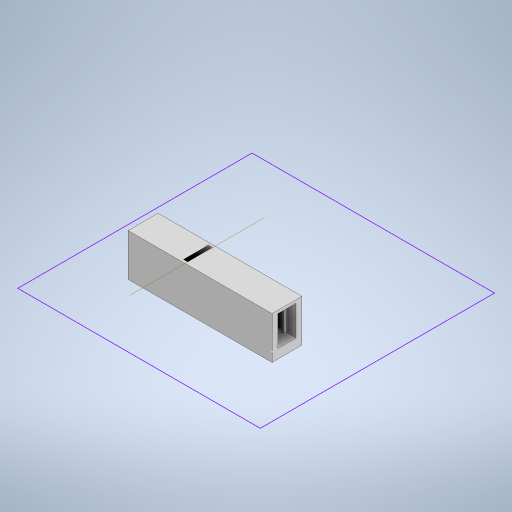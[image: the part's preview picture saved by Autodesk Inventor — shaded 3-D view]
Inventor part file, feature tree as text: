
AUTODESK INVENTOR PART (.ipt)
format: ipt  version: 2023 (Build 270158000, 158)  size: 439,296 bytes
history: native  units: in
note: dims shown in document units (in); Inventor stores cm internally (conversion verified against a paired STEP export)
features: sketch x8, extrude x7, plane x1
ambient origin geometry x8: Origin, YZ Plane, XZ Plane, XY Plane, X Axis, Y Axis, Z Axis, Center Point
bodies: Solid1 (feature_tree)
feature tree (16):
  extrude  "Extrusion1"  Depth=1.25in
  extrude  "Extrusion2"  Depth=0.55in
  extrude  "Extrusion3"  Depth=0.07in TaperAngle=0.0deg
  extrude  "Extrusion4"  TaperAngle=0.0deg  [1 undecoded]
  extrude  "Extrusion5"  Depth=0.0625in
  extrude  "Extrusion6"  Depth=0.25in
  plane  "Work Plane1"
  extrude  "Extrusion7"  Depth=0.1in
  sketch  "Sketch8"  dims[d17=0.1in d18=0.1in d19=0.1in d20=0.1in d21=1.0in d22=0.1in d23=0.1in d24=0.1in d25=0.1in d26=0.1in d27=0.1in d28=0.1in d29=0.1in d30=0.1in d31=0.1in d32=0.1in d33=0.1in d34=1.0in d35=1.0in d36=1.0in d37=1.25in d38=0.0in d39=0.1in d40=0.1in d41=0.1in d42=0.1in d43=0.1in d44=0.1in d45=1.0in d46=1.0in d47=0.1in d48=0.1in d49=1.0in d50=0.1in d51=0.1in d52=1.0in d53=1.25in d54=0.0in d55=0.125in d56=0.0in d57=45.0deg d58=0.0in d59=5.0in d60=0.125in d61=0.0in d62=0.5in d63=0.0344in]
  sketch  "Sketch1"  dims[d0=6.0in d1=1.25in]
  sketch  "Sketch2"  dims[d2=1.2in d3=0.55in]
  sketch  "Sketch3"  dims[d4=1.0in d5=0.07in d6=0.0in]
  sketch  "Sketch4"  dims[d7=1.2in d8=0.0in]
  sketch  "Sketch5"  dims[d9=0.07in d10=0.0in d11=0.0625in]
  sketch  "Sketch6"  dims[d12=0.25in d13=0.0in d14=0.25in]
  sketch  "Sketch7"  dims[d15=0.1in d16=0.1in]
note: 1 required parameter value undecoded (feature->parameter linkage not recoverable at this tier; creation-order binding heuristic only, values carry confidence <= 0.55)
